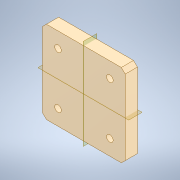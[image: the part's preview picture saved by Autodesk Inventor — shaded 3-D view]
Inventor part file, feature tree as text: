
AUTODESK INVENTOR PART (.ipt)
format: ipt  version: 2022 (Build 260153000, 153)  size: 123,904 bytes
history: native  units: mm
features: plane x2, sketch x2, extrude x1, chamfer x1, hole x1
ambient origin geometry x8: Origin, YZ Plane, XZ Plane, XY Plane, X Axis, Y Axis, Z Axis, Center Point
bodies: Solid1 (feature_tree)
feature tree (7):
  extrude  "Extrusion1"  Depth=43.0mm
  chamfer  "Chamfer1"  Distance=6.35mm
  hole  "Hole1"  [1 undecoded]
  plane  "Work Plane1"
  plane  "Work Plane2"
  sketch  "Sketch1"  dims[d0=43.0mm d1=43.0mm d2=6.35mm d3=0.0mm]
  sketch  "Sketch2"  dims[d4=2.0mm d5=2.0mm d6=45.0deg d7=8.0mm d8=8.0mm d9=8.0mm d10=8.0mm d11=8.0mm d12=8.0mm d13=3.4mm d14=6.0mm d15=6.3mm d16=2.0mm d17=90.0deg d18=7.0mm d19=20.594885mm]
note: 1 required parameter value undecoded (feature->parameter linkage not recoverable at this tier; creation-order binding heuristic only, values carry confidence <= 0.55)
